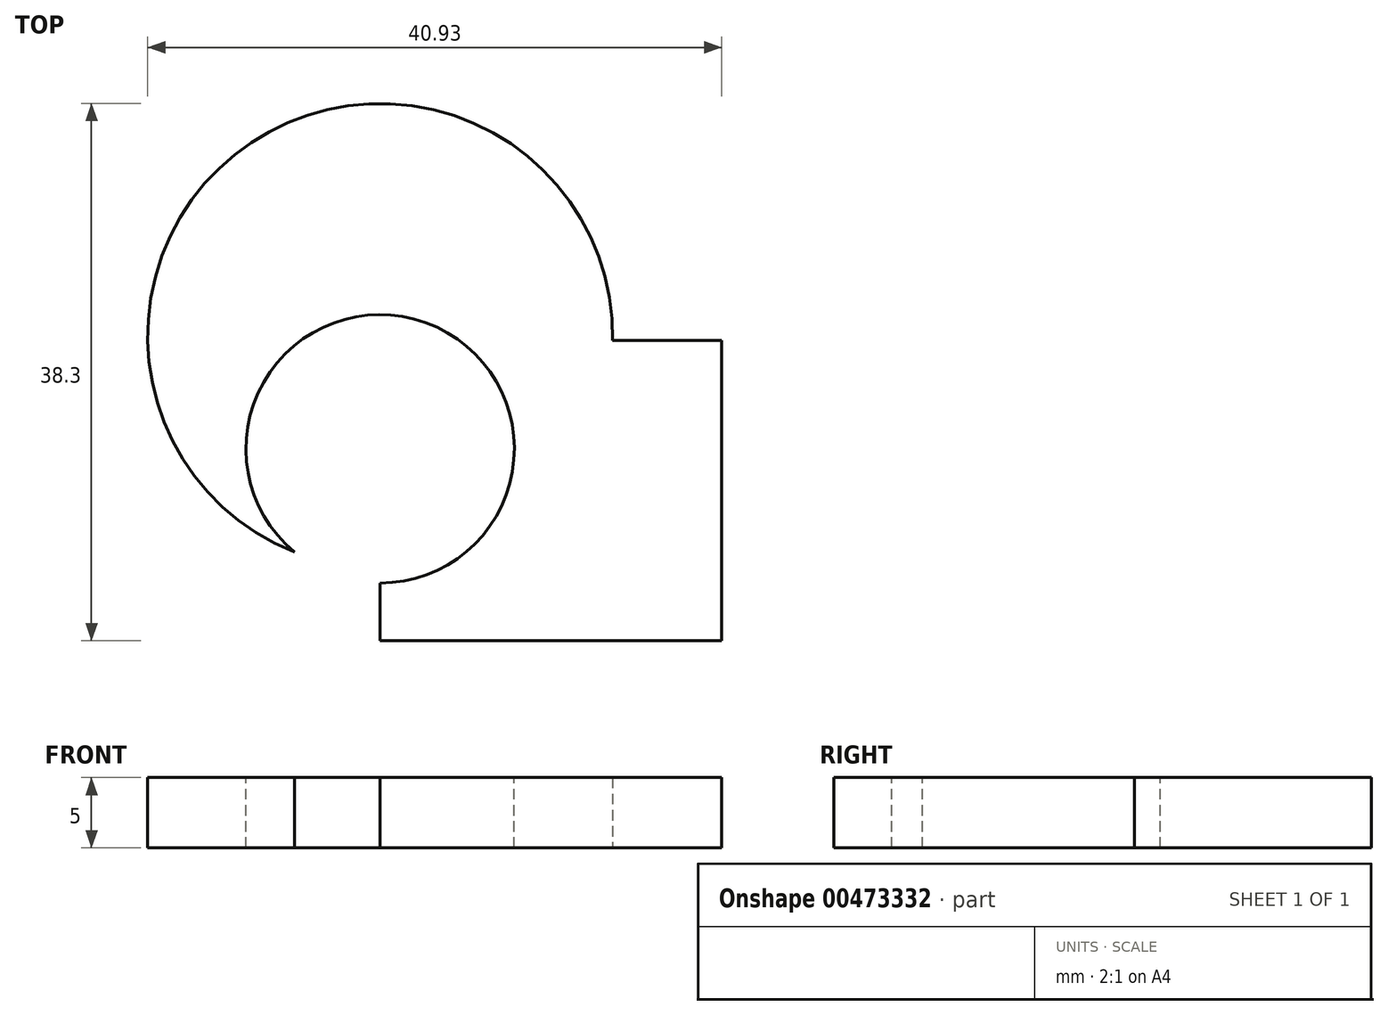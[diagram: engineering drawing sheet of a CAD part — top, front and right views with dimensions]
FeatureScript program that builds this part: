
annotation { "Feature Type Name" : "Feature", "Feature Type Description" : "" }
export const myFeature = defineFeature(function(context is Context, id is Id, definition is map)
    precondition{}
    {
        {
            var Q0;
            Q0=qCreatedBy(makeId("Top.planeOp"),FACE);
            var sketch = newSketch(context, id + "F0", { "sketchPlane" : qUnion([Q0])});
            skLineSegment(sketch, "E0.bottom", {"start": v(0, 0) * mm, "end": v(24.36, 0) * mm});
            skLineSegment(sketch, "E0.top", {"start": v(0, -21.41) * mm, "end": v(24.36, -21.41) * mm});
            skLineSegment(sketch, "E0.left", {"start": v(0, 0) * mm, "end": v(0, -21.41) * mm});
            skLineSegment(sketch, "E0.right", {"start": v(24.36, 0) * mm, "end": v(24.36, -21.41) * mm});
            skSolve(sketch);
        }
        {
            var Q0;
            Q0 = qSketchRegion(id + "F0", true);
            extrude(context, id + "F1", {"entities" : qUnion([Q0]), "depth" : 5 * mm});
        }
        {
            var Q0;
            Q0=qCreatedBy(makeId("Top.planeOp"),FACE);
            var sketch = newSketch(context, id + "F2", { "sketchPlane" : qUnion([Q0])});
            skCircle(sketch, "E1", {"center": v(0, 0.31) * mm, "radius": 16.57 * mm});
            skSolve(sketch);
        }
        {
            var Q0;
            Q0 = qSketchRegion(id + "F2", true);
            extrude(context, id + "F3", {"entities" : qUnion([Q0]), "operationType" : NewBodyOperationType.ADD, "depth" : 5 * mm});
        }
        {
            var Q0;
            Q0=makeQuery(id+"F3.boolean.opBoolean","MERGE",FACE,{"derivedFrom":[makeQuery(id+"F1.opExtrude","CAP_FACE",FACE,{"disambiguationData":[OSD([sQuery(id+"F0.wireOp",EDGE,"E0.bottom"),sQuery(id+"F0.wireOp",EDGE,"E0.top"),sQuery(id+"F0.wireOp",EDGE,"E0.left"),sQuery(id+"F0.wireOp",EDGE,"E0.right")])],"isStart":false}),makeQuery(id+"F3.opExtrude","CAP_FACE",FACE,{"disambiguationData":[OSD([sQuery(id+"F2.wireOp",EDGE,"E1")])],"isStart":false})]});
            var sketch = newSketch(context, id + "F4", { "sketchPlane" : qUnion([Q0])});
            skCircle(sketch, "E2", {"center": v(0, -7.73) * mm, "radius": 9.57 * mm});
            skSolve(sketch);
        }
        {
            var Q0;
            Q0 = qSketchRegion(id + "F4", true);
            extrude(context, id + "F5", {"entities" : qUnion([Q0]), "operationType" : NewBodyOperationType.REMOVE, "oppositeDirection" : true, "depth" : 6 * mm});
        }
    });
